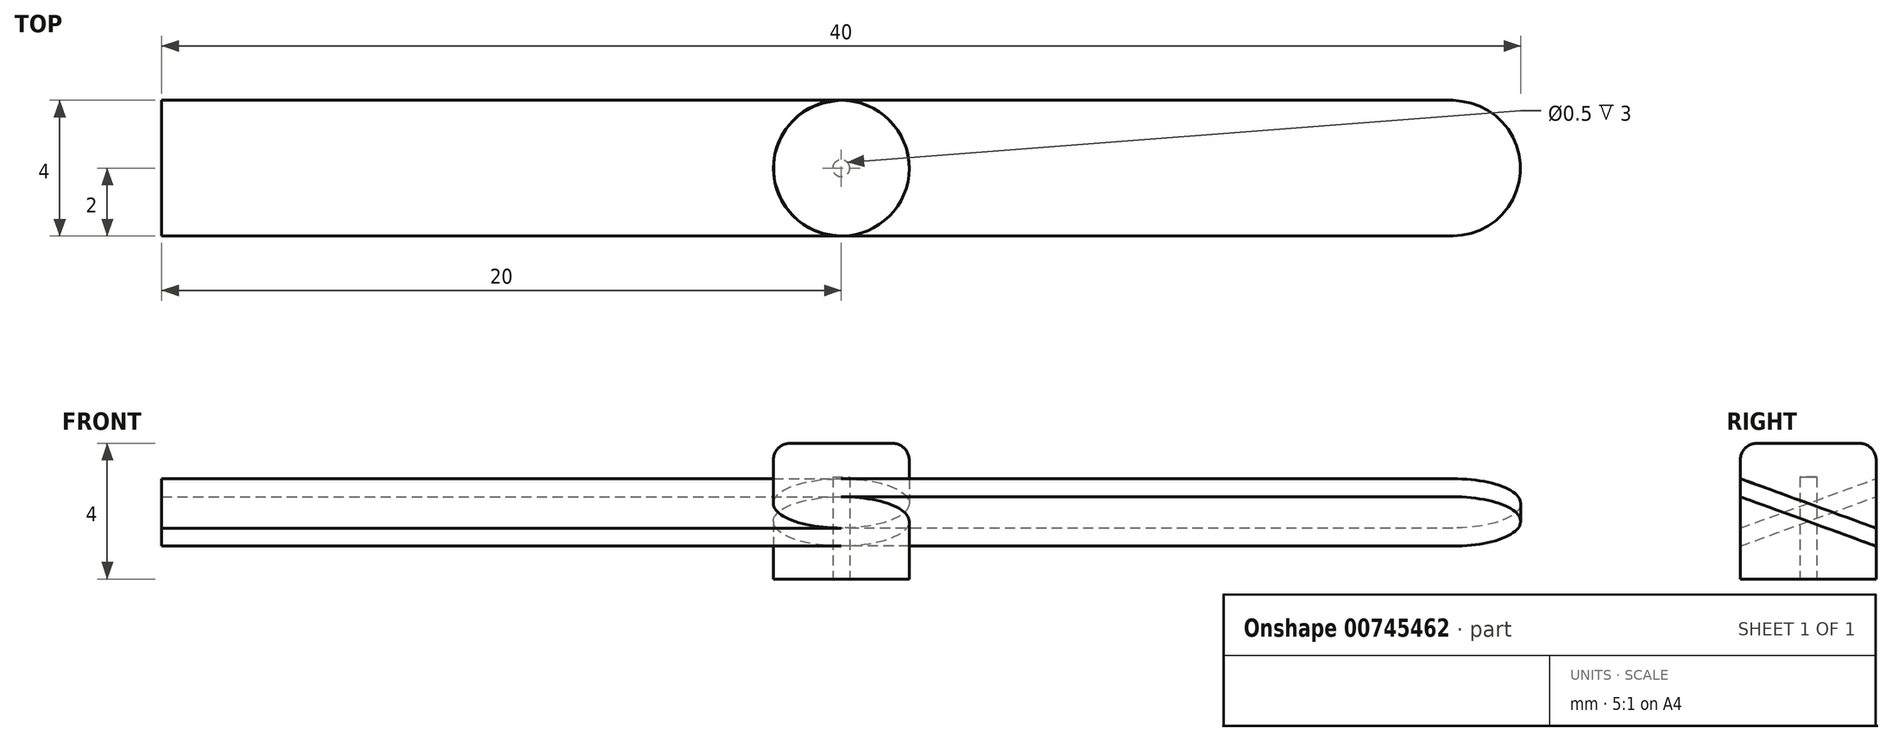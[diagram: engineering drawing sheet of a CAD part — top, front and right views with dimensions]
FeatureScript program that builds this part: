
annotation { "Feature Type Name" : "Feature", "Feature Type Description" : "" }
export const myFeature = defineFeature(function(context is Context, id is Id, definition is map)
    precondition{}
    {
        {
            var Q0;
            Q0=qCreatedBy(makeId("Top.planeOp"),FACE);
            var sketch = newSketch(context, id + "F0", { "sketchPlane" : qUnion([Q0])});
            skCircle(sketch, "E0", {"center": v(0, 0) * mm, "radius": 2 * mm});
            skSolve(sketch);
        }
        {
            var Q0;
            Q0=makeQuery(id+"F0.imprint","IMPRINT",FACE,{"disambiguationData":[TD([[makeQuery(id+"F0.imprint","IMPRINT",EDGE,{"derivedFrom":sQuery(id+"F0.wireOp",EDGE,"E0")}),1.0]])]});
            extrude(context, id + "F1", {"entities" : qUnion([Q0]), "depth" : 4 * mm, "offsetDistance" : 25 * mm});
        }
        {
            var Q0;
            Q0=qCreatedBy(makeId("Right.planeOp"),FACE);
            var sketch = newSketch(context, id + "F2", { "sketchPlane" : qUnion([Q0])});
            skLineSegment(sketch, "E1", {"start": v(-2, 0.3) * mm, "end": v(-2, 5.61) * mm, "construction": true});
            skLineSegment(sketch, "E2", {"start": v(2, 4) * mm, "end": v(2, 1.5) * mm, "construction": true});
            skLineSegment(sketch, "E3", {"start": v(-2, 2.96) * mm, "end": v(2, 1.5) * mm});
            skLineSegment(sketch, "E4", {"start": v(-2, 2.42) * mm, "end": v(2, 0.97) * mm});
            skLineSegment(sketch, "E5", {"start": v(-2, 2.96) * mm, "end": v(-2, 2.42) * mm});
            skLineSegment(sketch, "E6", {"start": v(2, 1.5) * mm, "end": v(2, 0.97) * mm});
            skSolve(sketch);
        }
        {
            var Q0;
            Q0=qSketchRegion(id+"F2",true);
            extrude(context, id + "F3", {"entities" : qUnion([Q0]), "operationType" : NewBodyOperationType.ADD, "depth" : 20 * mm, "offsetDistance" : 25 * mm});
        }
        {
            var Q0;
            Q0=qCreatedBy(makeId("Right.planeOp"),FACE);
            var sketch = newSketch(context, id + "F4", { "sketchPlane" : qUnion([Q0])});
            skLineSegment(sketch, "E7", {"start": v(2, 5.91) * mm, "end": v(2, 0) * mm});
            skLineSegment(sketch, "E8", {"start": v(-2, 0) * mm, "end": v(-2, 4) * mm});
            skLineSegment(sketch, "E9", {"start": v(2, 4) * mm, "end": v(2, 0) * mm, "construction": true});
            skLineSegment(sketch, "E10", {"start": v(-2, 0) * mm, "end": v(-2, 4) * mm, "construction": true});
            skLineSegment(sketch, "E11", {"start": v(-2, 1.5) * mm, "end": v(2, 2.96) * mm});
            skLineSegment(sketch, "E12", {"start": v(-2, 0.97) * mm, "end": v(2, 2.42) * mm});
            skLineSegment(sketch, "E13", {"start": v(2, 2.42) * mm, "end": v(2, 2.96) * mm});
            skLineSegment(sketch, "E14", {"start": v(-2, 0.97) * mm, "end": v(-2, 1.5) * mm});
            skSolve(sketch);
        }
        {
            var Q0;
            Q0=qSketchRegion(id+"F4",true);
            extrude(context, id + "F5", {"entities" : qUnion([Q0]), "operationType" : NewBodyOperationType.ADD, "oppositeDirection" : true, "depth" : 20 * mm, "offsetDistance" : 25 * mm});
        }
        {
            var Q0;
            Q0=makeQuery(id+"F5.opExtrude","CAP_EDGE",EDGE,{"disambiguationData":[OSD([sQuery(id+"F4.wireOp",EDGE,"E13")])],"isStart":false});
            var Q1;
            Q1=makeQuery(id+"F5.opExtrude","CAP_EDGE",EDGE,{"disambiguationData":[OSD([sQuery(id+"F4.wireOp",EDGE,"E14")])],"isStart":false});
            var Q2;
            Q2=makeQuery(id+"F3.opExtrude","CAP_EDGE",EDGE,{"disambiguationData":[OSD([sQuery(id+"F2.wireOp",EDGE,"E5")])],"isStart":false});
            var Q3;
            Q3=makeQuery(id+"F3.opExtrude","CAP_EDGE",EDGE,{"disambiguationData":[OSD([sQuery(id+"F2.wireOp",EDGE,"E6")])],"isStart":false});
            fillet(context, id + "F6", {"entities" : qUnion([Q0, Q1, Q2, Q3]), "radius" : 2 * mm, "tangentPropagation" : true, "allowEdgeOverflow" : false});
        }
        {
            var Q0;
            Q0=makeQuery(id+"F1.opExtrude","CAP_EDGE",EDGE,{"disambiguationData":[OSD([sQuery(id+"F0.wireOp",EDGE,"E0")])],"isStart":false});
            fillet(context, id + "F7", {"entities" : qUnion([Q0]), "radius" : 0.5 * mm, "tangentPropagation" : true, "allowEdgeOverflow" : false});
        }
        {
            var Q0;
            Q0=makeQuery(id+"F1.opExtrude","CAP_FACE",FACE,{"disambiguationData":[OSD([sQuery(id+"F0.wireOp",EDGE,"E0")])],"isStart":true});
            var sketch = newSketch(context, id + "F8", { "sketchPlane" : qUnion([Q0])});
            skCircle(sketch, "E15", {"center": v(0, 0) * mm, "radius": 0.25 * mm});
            skSolve(sketch);
        }
        {
            var Q0;
            Q0=makeQuery(id+"F8.imprint","IMPRINT",FACE,{"disambiguationData":[TD([[makeQuery(id+"F8.imprint","IMPRINT",EDGE,{"derivedFrom":sQuery(id+"F8.wireOp",EDGE,"E15")}),1.0]])]});
            extrude(context, id + "F9", {"entities" : qUnion([Q0]), "operationType" : NewBodyOperationType.REMOVE, "oppositeDirection" : true, "depth" : 3 * mm, "offsetDistance" : 25 * mm});
        }
    });
